# Revit family: FCSG25N
name_source: partatom
category: Generic Models
revit_build: Autodesk Revit LT 2017 (Build: 20170118_1100(x64)
units: mm (PartAtom-declared; Revit-internal decimal feet)

## family parameters
Always vertical = No
Can host rebar = No
Cut with Voids When Loaded = No
Part Type = Normal
Room Calculation Point = No
Round Connector Dimension = Use Diameter
Shared = No
Work Plane-Based = Yes

## types (1)
- NBS Standard Parameters
    AssetType = Fixed
    BIMObjectName = Metpro_Metprolibrary_Flexiconduit_Conduitaccessories
    Color = Brass
    Default Elevation = 1219 mm
    Description = FCSG25N - 25mm Swivel Adaptor
    DurationUnit = 1 Year
    Finish = Nickel Plated
    Keynote = IP54 Rated
    Manufacturer = Metpro Limited
    ManufacturerName = Metpro ltd
    ManufacturerURL = www.metpro.co.uk
    Material = Brass
    ModelNumber = FCSG25N
    ModelReference = Flexiconduit fittings
    NBSDescription = Flexible Conduit
    NBSReference = 90-55-10/360
    Name = FCSG25N - FLEXICONDUIT ADAPTOR
    NominalHeight = 30 mm  [stored 0.0984252 ft]
    NominalLength = 40 mm  [stored 0.131234 ft]
    NominalWidth = 30 mm  [stored 0.0984252 ft]
    ProductInformation = www.metpro.co.uk/pdf/FCSG25N.pdf
    Shape = Circular
    Size = 25mm
    URL = www.metpro.co.uk
    Uniclass2 = Pr_65_70_11_30
    Version = 1
    WarrantyDurationUnit = 12 Months
    WarrantyGuarantorParts = 12 Months
    Weight = 0.076kg

note: [stored X ft] marks values corroborated as IEEE doubles in the binary element streams (Revit-internal decimal feet)

## geometry (parser evidence)
native form markers: Sweep x3
no freeform markers — native parametric forms only
